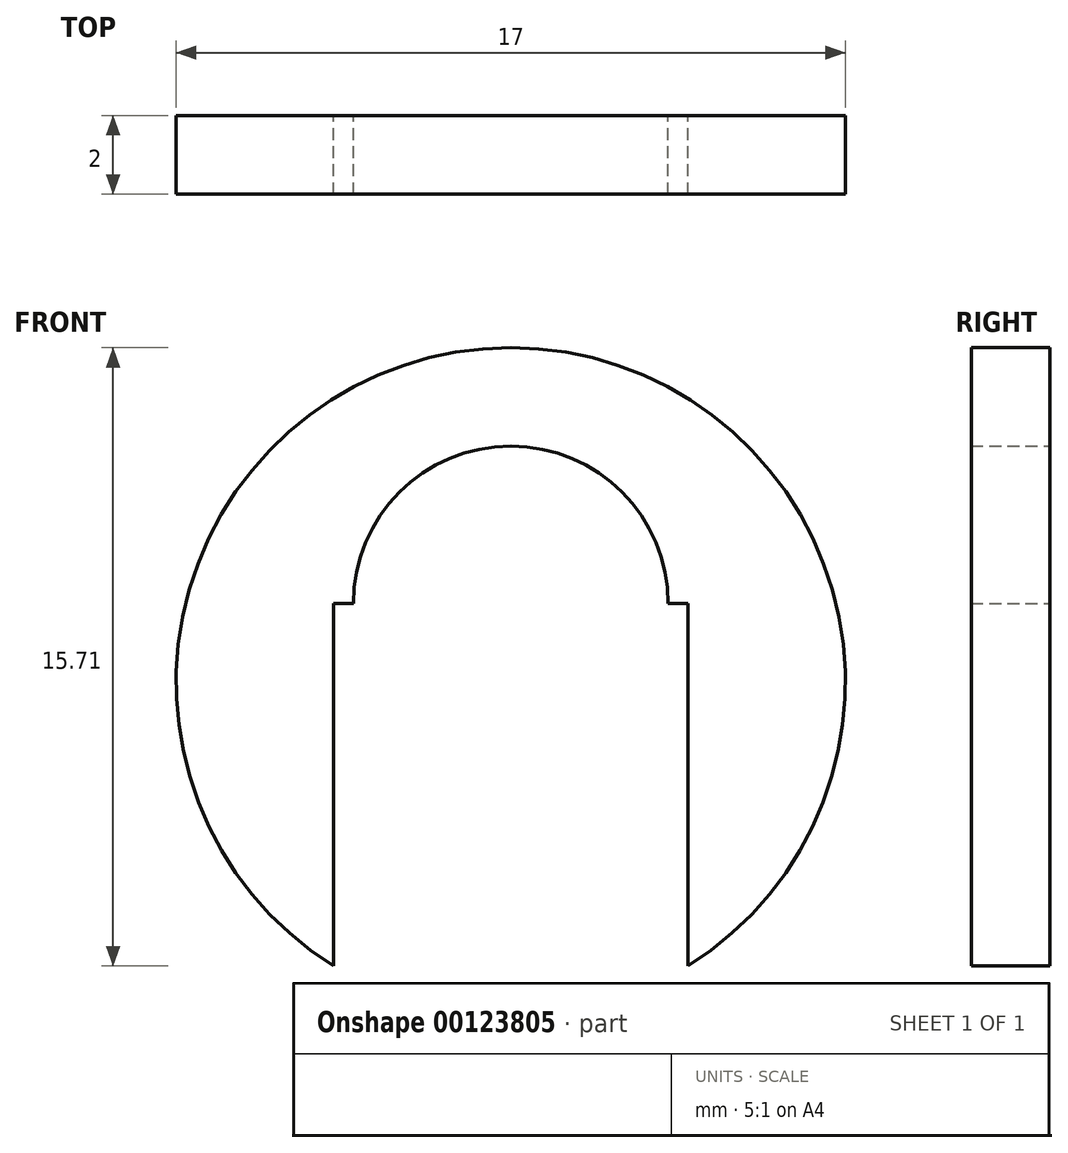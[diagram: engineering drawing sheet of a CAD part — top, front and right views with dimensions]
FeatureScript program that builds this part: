
annotation { "Feature Type Name" : "Feature", "Feature Type Description" : "" }
export const myFeature = defineFeature(function(context is Context, id is Id, definition is map)
    precondition{}
    {
        {
            var Q0;
            Q0=qCreatedBy(makeId("Front.planeOp"),FACE);
            var sketch = newSketch(context, id + "F0", { "sketchPlane" : qUnion([Q0])});
            skArc(sketch, "E0", {"start": v(-4, 2) * mm, "mid": v(0, 6) * mm, "end": v(4, 2) * mm});
            skLineSegment(sketch, "E1", {"start": v(-4, 2) * mm, "end": v(-4.5, 2) * mm});
            skLineSegment(sketch, "E2", {"start": v(-4.5, 2) * mm, "end": v(-4.5, -4.5) * mm});
            skLineSegment(sketch, "E3", {"start": v(4.5, -4.5) * mm, "end": v(4.5, 2) * mm});
            skLineSegment(sketch, "E4", {"start": v(4.5, 2) * mm, "end": v(4, 2) * mm});
            skLineSegment(sketch, "E5", {"start": v(0, -3.6) * mm, "end": v(0, 7.92) * mm, "construction": true});
            skPoint(sketch, "E5.endSnap0", {"position": v(0, 6) * mm});
            skLineSegment(sketch, "E6", {"start": v(-4, 2) * mm, "end": v(4, 2) * mm, "construction": true});
            skArc(sketch, "E7", {"start": v(4.5, -7.21) * mm, "mid": v(0, 8.5) * mm, "end": v(-4.5, -7.21) * mm});
            skLineSegment(sketch, "E8", {"start": v(-4.5, -4.5) * mm, "end": v(-4.5, -7.21) * mm});
            skLineSegment(sketch, "E9", {"start": v(4.5, -4.5) * mm, "end": v(4.5, -7.21) * mm});
            skSolve(sketch);
        }
        {
            var Q0;
            Q0 = qSketchRegion(id + "F0", true);
            extrude(context, id + "F1", {"entities" : qUnion([Q0]), "depth" : 2 * mm});
        }
    });
